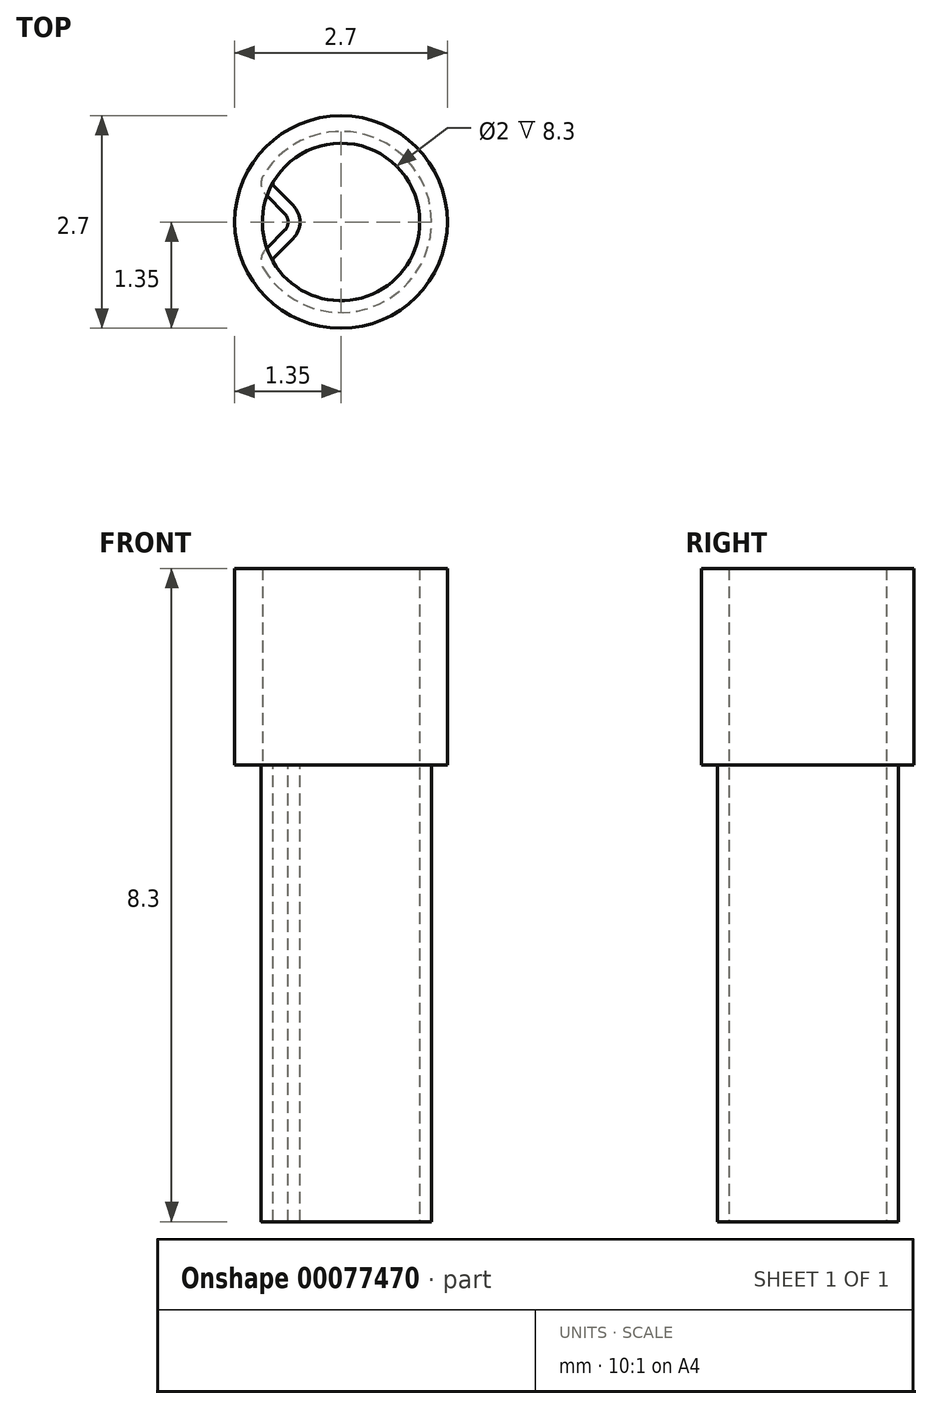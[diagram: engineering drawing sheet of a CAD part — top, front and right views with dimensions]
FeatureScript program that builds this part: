
annotation { "Feature Type Name" : "Feature", "Feature Type Description" : "" }
export const myFeature = defineFeature(function(context is Context, id is Id, definition is map)
    precondition{}
    {
        {
            var Q0;
            Q0=qCreatedBy(makeId("Top.planeOp"),FACE);
            var sketch = newSketch(context, id + "F0", { "sketchPlane" : qUnion([Q0])});
            skCircle(sketch, "E0", {"center": v(0, 0) * mm, "radius": 1.35 * mm});
            skCircle(sketch, "E1", {"center": v(0, 0) * mm, "radius": 1 * mm});
            skSolve(sketch);
        }
        {
            var Q0;
            Q0=makeQuery(id+"F0.imprint","IMPRINT",FACE,{"disambiguationData":[TD([[makeQuery(id+"F0.imprint","IMPRINT",EDGE,{"derivedFrom":sQuery(id+"F0.wireOp",EDGE,"E0")}),1.0]])]});
            extrude(context, id + "F1", {"entities" : qUnion([Q0]), "depth" : 2 * mm});
        }
        {
            var Q0;
            Q0=makeQuery(id+"F1.opExtrude","CAP_FACE",FACE,{"disambiguationData":[OSD([sQuery(id+"F0.wireOp",EDGE,"E0"),sQuery(id+"F0.wireOp",EDGE,"E1")])],"isStart":true});
            var sketch = newSketch(context, id + "F2", { "sketchPlane" : qUnion([Q0])});
            skArc(sketch, "E2", {"start": v(-0.86, -0.51) * mm, "mid": v(1, 0) * mm, "end": v(-0.86, 0.51) * mm});
            skArc(sketch, "E3", {"start": v(-0.99, -0.6) * mm, "mid": v(1.15, 0) * mm, "end": v(-0.99, 0.6) * mm});
            skLineSegment(sketch, "E4", {"start": v(0, 0) * mm, "end": v(-0.61, 0) * mm, "construction": true});
            skLineSegment(sketch, "E5", {"start": v(-0.72, 0.1) * mm, "end": v(-0.96, 0.35) * mm});
            skLineSegment(sketch, "E6", {"start": v(-0.72, -0.1) * mm, "end": v(-0.96, -0.35) * mm});
            skLineSegment(sketch, "E7", {"start": v(-0.85, 0.45) * mm, "end": v(-0.6, 0.21) * mm});
            skLineSegment(sketch, "E8", {"start": v(-0.6, -0.21) * mm, "end": v(-0.85, -0.45) * mm});
            skPoint(sketch, "E9.visualSharp", {"position": v(-1.06, 0.45) * mm});
            skArc(sketch, "E9.filletArc", {"start": v(-0.99, 0.6) * mm, "mid": v(-1.01, 0.46) * mm, "end": v(-0.96, 0.35) * mm});
            skPoint(sketch, "E10.visualSharp", {"position": v(-1.06, -0.45) * mm});
            skArc(sketch, "E10.filletArc", {"start": v(-0.96, -0.35) * mm, "mid": v(-1.01, -0.46) * mm, "end": v(-0.99, -0.6) * mm});
            skPoint(sketch, "E11.visualSharp", {"position": v(-0.6, 0) * mm});
            skArc(sketch, "E11.filletArc", {"start": v(-0.72, -0.1) * mm, "mid": v(-0.67, 0) * mm, "end": v(-0.72, 0.1) * mm});
            skPoint(sketch, "E12.visualSharp", {"position": v(-0.4, 0) * mm});
            skArc(sketch, "E12.filletArc", {"start": v(-0.6, -0.21) * mm, "mid": v(-0.52, 0) * mm, "end": v(-0.61, 0.21) * mm});
            skPoint(sketch, "E13.visualSharp", {"position": v(-0.88, 0.48) * mm});
            skArc(sketch, "E13.filletArc", {"start": v(-0.86, 0.51) * mm, "mid": v(-0.86, 0.48) * mm, "end": v(-0.85, 0.45) * mm});
            skPoint(sketch, "E14.visualSharp", {"position": v(-0.88, -0.48) * mm});
            skArc(sketch, "E14.filletArc", {"start": v(-0.85, -0.45) * mm, "mid": v(-0.86, -0.48) * mm, "end": v(-0.86, -0.51) * mm});
            skSolve(sketch);
        }
        {
            var Q0;
            Q0=makeQuery(id+"F2.imprint","IMPRINT",FACE,{"disambiguationData":[TD([[makeQuery(id+"F2.imprint","IMPRINT",EDGE,{"derivedFrom":sQuery(id+"F2.wireOp",EDGE,"E7")}),-1.0]])]});
            var Q1;
            {var subQ3=sQuery(id+"F2.wireOp",EDGE,"E2");Q1=makeQuery(id+"F2.imprint","IMPRINT",FACE,{"disambiguationData":[TD([[makeQuery(id+"F2.imprint","IMPRINT",EDGE,{"derivedFrom":subQ3}),1.0]])]});}
            extrude(context, id + "F3", {"entities" : qUnion([Q0, Q1]), "operationType" : NewBodyOperationType.ADD, "depth" : 2.5 * mm});
        }
        {
            var Q0;
            Q0=makeQuery(id+"F0.imprint","IMPRINT",FACE,{"disambiguationData":[TD([[makeQuery(id+"F0.imprint","IMPRINT",EDGE,{"derivedFrom":sQuery(id+"F0.wireOp",EDGE,"E0")}),1.0]])]});
            extrude(context, id + "F4", {"entities" : qUnion([Q0]), "depth" : 2 * mm});
        }
        {
            var Q0;
            {var subQ3=sQuery(id+"F2.wireOp",EDGE,"E2");Q0=makeQuery(id+"F2.imprint","IMPRINT",FACE,{"disambiguationData":[TD([[makeQuery(id+"F2.imprint","IMPRINT",EDGE,{"derivedFrom":subQ3}),1.0]])]});}
            var Q1;
            Q1=makeQuery(id+"F2.imprint","IMPRINT",FACE,{"disambiguationData":[TD([[makeQuery(id+"F2.imprint","IMPRINT",EDGE,{"derivedFrom":sQuery(id+"F2.wireOp",EDGE,"E7")}),-1.0]])]});
            extrude(context, id + "F5", {"entities" : qUnion([Q0, Q1]), "operationType" : NewBodyOperationType.ADD, "depth" : 4.7 * mm});
        }
        {
            var Q0;
            Q0=makeQuery(id+"F0.imprint","IMPRINT",FACE,{"disambiguationData":[TD([[makeQuery(id+"F0.imprint","IMPRINT",EDGE,{"derivedFrom":sQuery(id+"F0.wireOp",EDGE,"E0")}),1.0]])]});
            extrude(context, id + "F6", {"entities" : qUnion([Q0]), "depth" : 1.5 * mm});
        }
        {
            var Q0;
            Q0=makeQuery(id+"F2.imprint","IMPRINT",FACE,{"disambiguationData":[TD([[makeQuery(id+"F2.imprint","IMPRINT",EDGE,{"derivedFrom":sQuery(id+"F2.wireOp",EDGE,"E7")}),-1.0]])]});
            var Q1;
            {var subQ3=sQuery(id+"F2.wireOp",EDGE,"E2");Q1=makeQuery(id+"F2.imprint","IMPRINT",FACE,{"disambiguationData":[TD([[makeQuery(id+"F2.imprint","IMPRINT",EDGE,{"derivedFrom":subQ3}),1.0]])]});}
            extrude(context, id + "F7", {"entities" : qUnion([Q0, Q1]), "operationType" : NewBodyOperationType.ADD, "depth" : 4.8 * mm});
        }
        {
            var Q0;
            Q0=makeQuery(id+"F0.imprint","IMPRINT",FACE,{"disambiguationData":[TD([[makeQuery(id+"F0.imprint","IMPRINT",EDGE,{"derivedFrom":sQuery(id+"F0.wireOp",EDGE,"E0")}),1.0]])]});
            extrude(context, id + "F8", {"entities" : qUnion([Q0]), "depth" : 2 * mm});
        }
        {
            var Q0;
            Q0=makeQuery(id+"F2.imprint","IMPRINT",FACE,{"disambiguationData":[TD([[makeQuery(id+"F2.imprint","IMPRINT",EDGE,{"derivedFrom":sQuery(id+"F2.wireOp",EDGE,"E7")}),-1.0]])]});
            var Q1;
            {var subQ3=sQuery(id+"F2.wireOp",EDGE,"E2");Q1=makeQuery(id+"F2.imprint","IMPRINT",FACE,{"disambiguationData":[TD([[makeQuery(id+"F2.imprint","IMPRINT",EDGE,{"derivedFrom":subQ3}),1.0]])]});}
            extrude(context, id + "F9", {"entities" : qUnion([Q0, Q1]), "operationType" : NewBodyOperationType.ADD, "depth" : 5.8 * mm});
        }
        {
            var Q0;
            Q0=makeQuery(id+"F0.imprint","IMPRINT",FACE,{"disambiguationData":[TD([[makeQuery(id+"F0.imprint","IMPRINT",EDGE,{"derivedFrom":sQuery(id+"F0.wireOp",EDGE,"E0")}),1.0]])]});
            extrude(context, id + "F10", {"entities" : qUnion([Q0]), "depth" : 2.5 * mm});
        }
        {
            var Q0;
            Q0=makeQuery(id+"F2.imprint","IMPRINT",FACE,{"disambiguationData":[TD([[makeQuery(id+"F2.imprint","IMPRINT",EDGE,{"derivedFrom":sQuery(id+"F2.wireOp",EDGE,"E7")}),-1.0]])]});
            var Q1;
            {var subQ3=sQuery(id+"F2.wireOp",EDGE,"E2");Q1=makeQuery(id+"F2.imprint","IMPRINT",FACE,{"disambiguationData":[TD([[makeQuery(id+"F2.imprint","IMPRINT",EDGE,{"derivedFrom":subQ3}),1.0]])]});}
            extrude(context, id + "F11", {"entities" : qUnion([Q0, Q1]), "operationType" : NewBodyOperationType.ADD, "depth" : 2.5 * mm});
        }
    });
